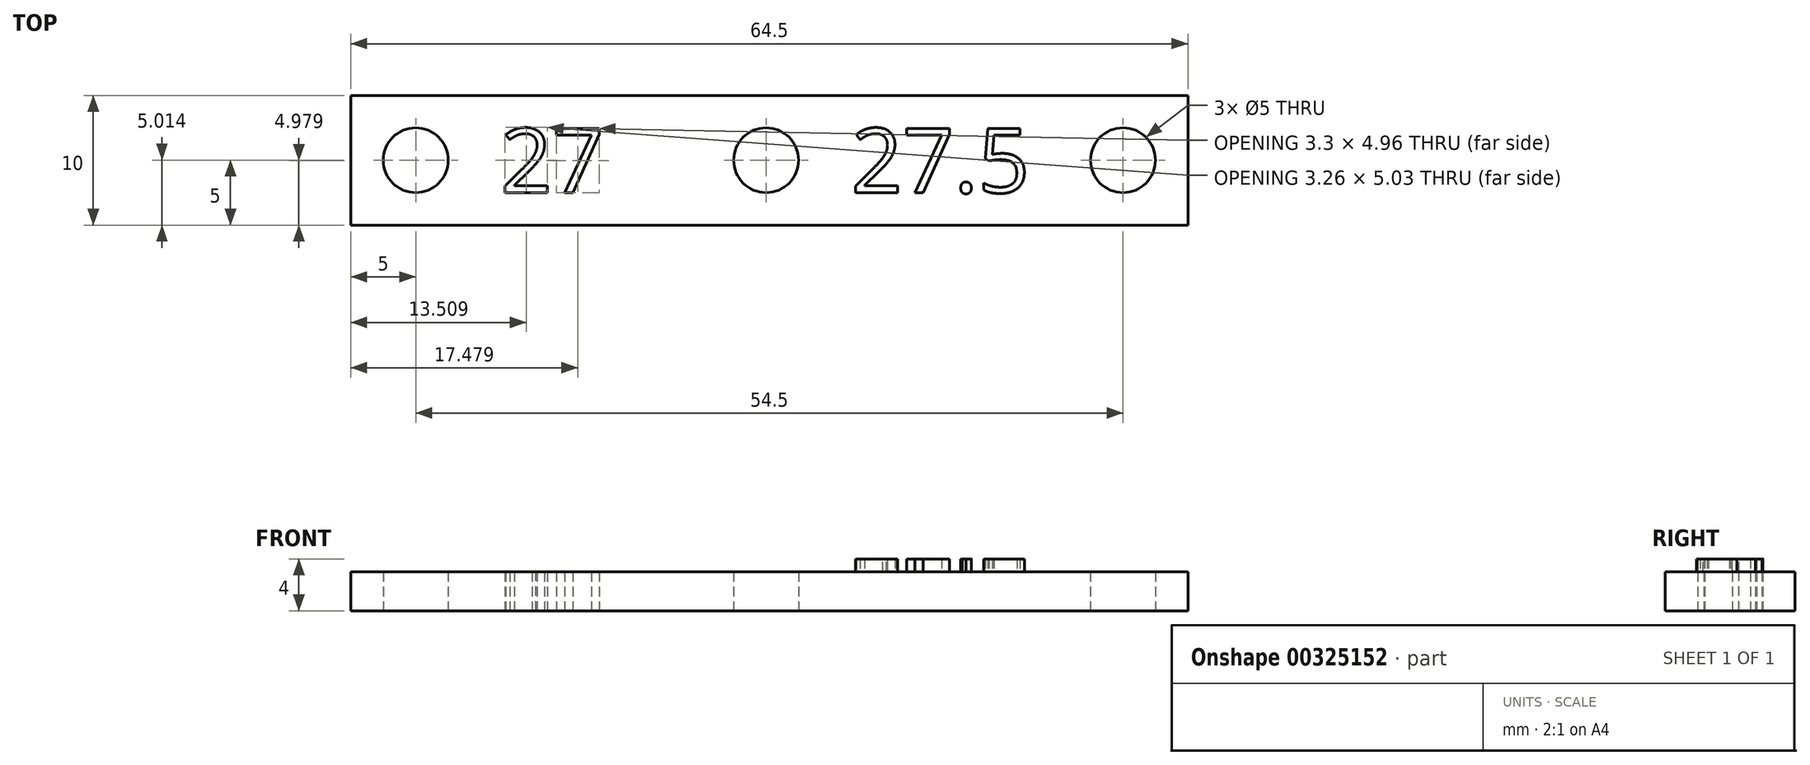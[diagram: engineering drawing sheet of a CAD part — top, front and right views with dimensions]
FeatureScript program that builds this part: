
annotation { "Feature Type Name" : "Feature", "Feature Type Description" : "" }
export const myFeature = defineFeature(function(context is Context, id is Id, definition is map)
    precondition{}
    {
        {
            var Q0;
            Q0=qCreatedBy(makeId("Top.planeOp"),FACE);
            var sketch = newSketch(context, id + "F0", { "sketchPlane" : qUnion([Q0])});
            skLineSegment(sketch, "E0", {"start": v(0, 0) * mm, "end": v(27.5, 0) * mm, "construction": true});
            skText(sketch, "E1", { "text": "27.5\n", "fontName": "OpenSans-Regular.ttf"});
            skCircle(sketch, "E2", {"center": v(0, 0) * mm, "radius": 2.5 * mm});
            skCircle(sketch, "E3", {"center": v(27.5, 0) * mm, "radius": 2.5 * mm});
            skLineSegment(sketch, "E4", {"start": v(0, 0) * mm, "end": v(-27, 0) * mm, "construction": true});
            skLineSegment(sketch, "E5", {"start": v(-27, 0) * mm, "end": v(-32, 0) * mm, "construction": true});
            skText(sketch, "E6", { "text": "27\n", "fontName": "OpenSans-Regular.ttf"});
            skLineSegment(sketch, "E7", {"start": v(0, 0) * mm, "end": v(6.54, 2.5) * mm, "construction": true});
            skLineSegment(sketch, "E8", {"start": v(0, 0) * mm, "end": v(6.54, -2.5) * mm, "construction": true});
            skLineSegment(sketch, "E9", {"start": v(-27, 0) * mm, "end": v(-20.46, 2.5) * mm, "construction": true});
            skLineSegment(sketch, "E10", {"start": v(-20.46, -2.5) * mm, "end": v(-27, 0) * mm, "construction": true});
            skCircle(sketch, "E11", {"center": v(-27, 0) * mm, "radius": 2.5 * mm});
            skLineSegment(sketch, "E12", {"start": v(-32, 0) * mm, "end": v(-32, 5) * mm});
            skLineSegment(sketch, "E13", {"start": v(-32, 0) * mm, "end": v(-32, -5) * mm});
            skLineSegment(sketch, "E14", {"start": v(27.5, 0) * mm, "end": v(32.5, 0) * mm, "construction": true});
            skLineSegment(sketch, "E15", {"start": v(32.5, 0) * mm, "end": v(32.5, 5) * mm});
            skLineSegment(sketch, "E16", {"start": v(32.5, 0) * mm, "end": v(32.5, -5) * mm});
            skLineSegment(sketch, "E17", {"start": v(32.5, 5) * mm, "end": v(-32, 5) * mm});
            skLineSegment(sketch, "E18", {"start": v(-32, -5) * mm, "end": v(32.5, -5) * mm});
            const initialGuessF0  = {"E1": [0.00654, -0.0025, 1, 0, 0.005], "E6": [-0.02046, -0.0025, 1, 0, 0.005]};
            skSetInitialGuess(sketch, initialGuessF0);
            skSolve(sketch);
        }
        {
            var Q0;
            Q0=makeQuery(id+"F0.imprint","IMPRINT",FACE,{"disambiguationData":[TD([[makeQuery(id+"F0.imprint","IMPRINT",EDGE,{"derivedFrom":sQuery(id+"F0.wireOp",EDGE,"E1.sketch_text.stroke-0")}),1.0]])]});
            extrude(context, id + "F1", {"entities" : qUnion([Q0]), "depth" : 3 * mm});
        }
        {
            var Q0;
            Q0=makeQuery(id+"F0.imprint","IMPRINT",FACE,{"disambiguationData":[TD([[makeQuery(id+"F0.imprint","IMPRINT",EDGE,{"derivedFrom":sQuery(id+"F0.wireOp",EDGE,"E1.sketch_text.stroke-0")}),-1.0]])]});
            var Q1;
            Q1=makeQuery(id+"F0.imprint","IMPRINT",FACE,{"disambiguationData":[TD([[makeQuery(id+"F0.imprint","IMPRINT",EDGE,{"derivedFrom":sQuery(id+"F0.wireOp",EDGE,"E1.sketch_text.stroke-27")}),-1.0]])]});
            var Q2;
            Q2=makeQuery(id+"F0.imprint","IMPRINT",FACE,{"disambiguationData":[TD([[makeQuery(id+"F0.imprint","IMPRINT",EDGE,{"derivedFrom":sQuery(id+"F0.wireOp",EDGE,"E1.sketch_text.stroke-35")}),-1.0]])]});
            var Q3;
            Q3=makeQuery(id+"F0.imprint","IMPRINT",FACE,{"disambiguationData":[TD([[makeQuery(id+"F0.imprint","IMPRINT",EDGE,{"derivedFrom":sQuery(id+"F0.wireOp",EDGE,"E1.sketch_text.stroke-20")}),-1.0]])]});
            extrude(context, id + "F2", {"entities" : qUnion([Q0, Q1, Q2, Q3]), "operationType" : NewBodyOperationType.ADD, "depth" : 4 * mm});
        }
    });
